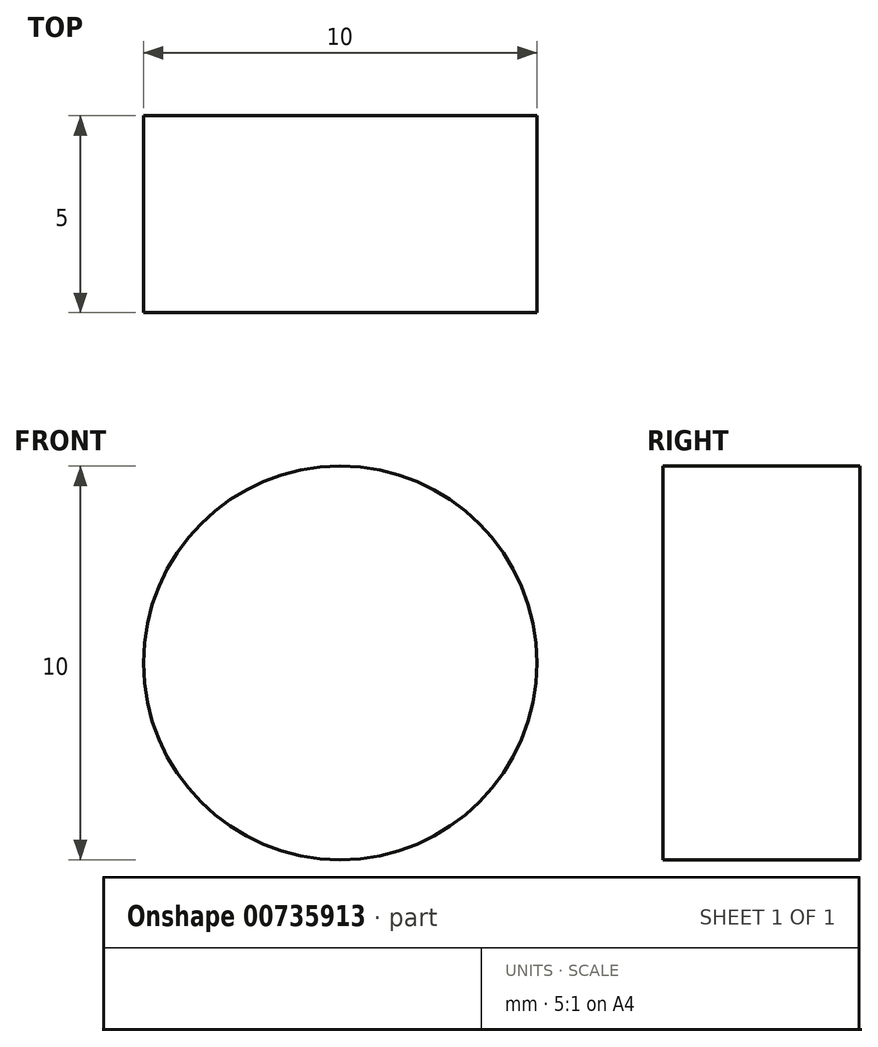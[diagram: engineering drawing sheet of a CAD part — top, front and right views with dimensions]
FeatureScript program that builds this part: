
annotation { "Feature Type Name" : "Feature", "Feature Type Description" : "" }
export const myFeature = defineFeature(function(context is Context, id is Id, definition is map)
    precondition{}
    {
        {
            var Q0;
            Q0=qCreatedBy(makeId("Front.planeOp"),FACE);
            var sketch = newSketch(context, id + "F0", { "sketchPlane" : qUnion([Q0])});
            skCircle(sketch, "E0", {"center": v(0, 0) * mm, "radius": 5 * mm});
            skSolve(sketch);
        }
        {
            var Q0;
            Q0 = qSketchRegion(id + "F0", true);
            extrude(context, id + "F1", {"entities" : qUnion([Q0]), "depth" : 5 * mm, "offsetDistance" : 25.4 * mm});
        }
    });
